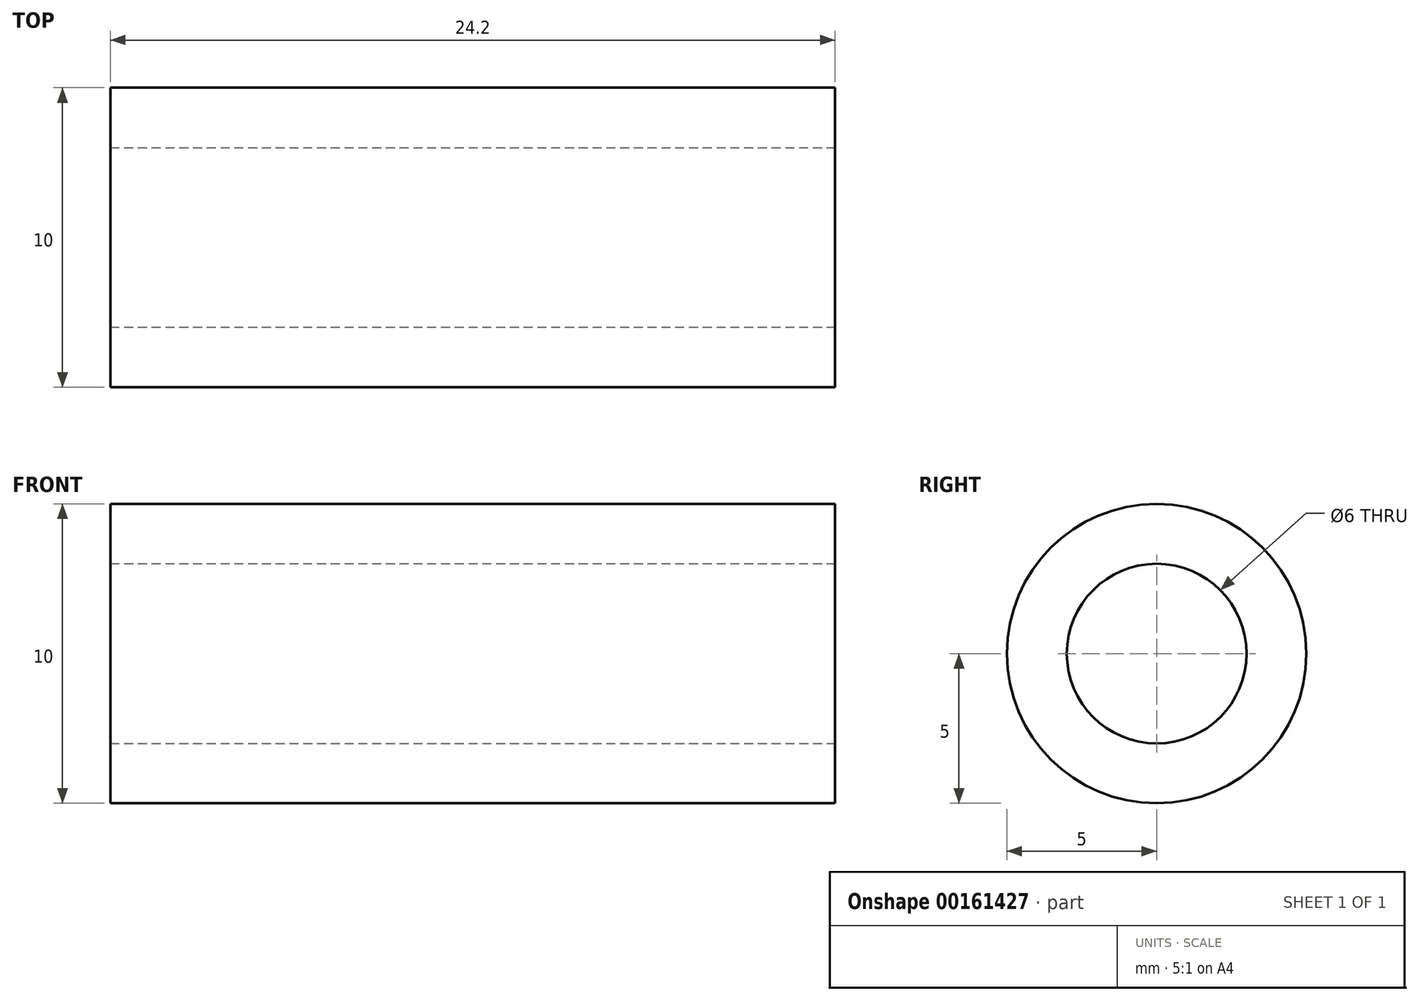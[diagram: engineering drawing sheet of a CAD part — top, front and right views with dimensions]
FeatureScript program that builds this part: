
annotation { "Feature Type Name" : "Feature", "Feature Type Description" : "" }
export const myFeature = defineFeature(function(context is Context, id is Id, definition is map)
    precondition{}
    {
        {
            var Q0;
            Q0=qCreatedBy(makeId("Right.planeOp"),FACE);
            var sketch = newSketch(context, id + "F0", { "sketchPlane" : qUnion([Q0])});
            skCircle(sketch, "E0", {"center": v(0, 0) * mm, "radius": 5 * mm});
            skCircle(sketch, "E1", {"center": v(0, 0) * mm, "radius": 3 * mm});
            skSolve(sketch);
        }
        {
            var Q0;
            Q0=makeQuery(id+"F0.imprint","IMPRINT",FACE,{"disambiguationData":[TD([[makeQuery(id+"F0.imprint","IMPRINT",EDGE,{"derivedFrom":sQuery(id+"F0.wireOp",EDGE,"E0")}),1.0]])]});
            extrude(context, id + "F1", {"entities" : qUnion([Q0]), "oppositeDirection" : true, "depth" : 24.2 * mm});
        }
    });
